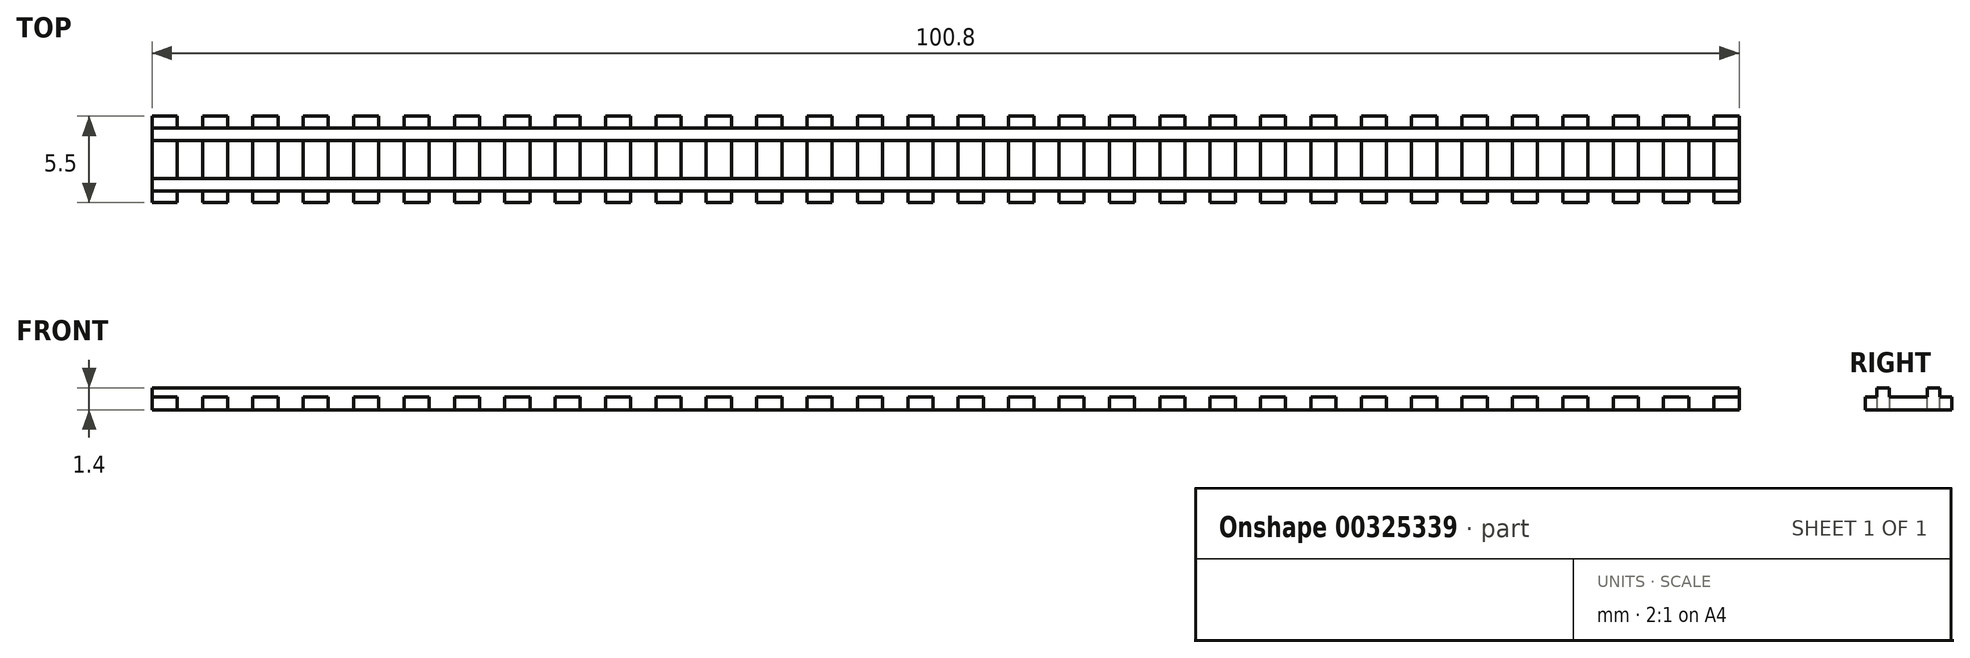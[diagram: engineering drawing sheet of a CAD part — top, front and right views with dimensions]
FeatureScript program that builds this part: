
annotation { "Feature Type Name" : "Feature", "Feature Type Description" : "" }
export const myFeature = defineFeature(function(context is Context, id is Id, definition is map)
    precondition{}
    {
        {
            var Q0;
            Q0=qCreatedBy(makeId("Top.planeOp"),FACE);
            var sketch = newSketch(context, id + "F0", { "sketchPlane" : qUnion([Q0])});
            skLineSegment(sketch, "E0.bottom", {"start": v(50.4, 2.8) * mm, "end": v(-50.4, 2.8) * mm});
            skLineSegment(sketch, "E0.top", {"start": v(50.4, 3.6) * mm, "end": v(-50.4, 3.6) * mm});
            skLineSegment(sketch, "E0.left", {"start": v(50.4, 2.8) * mm, "end": v(50.4, 3.6) * mm});
            skLineSegment(sketch, "E0.right", {"start": v(-50.4, 2.8) * mm, "end": v(-50.4, 3.6) * mm});
            skPoint(sketch, "E0.middle", {"position": v(0, 3.2) * mm});
            skLineSegment(sketch, "E1.bottom", {"start": v(50.4, -0.4) * mm, "end": v(-50.4, -0.4) * mm});
            skLineSegment(sketch, "E1.top", {"start": v(50.4, 0.4) * mm, "end": v(-50.4, 0.4) * mm});
            skLineSegment(sketch, "E1.left", {"start": v(50.4, -0.4) * mm, "end": v(50.4, 0.4) * mm});
            skLineSegment(sketch, "E1.right", {"start": v(-50.4, -0.4) * mm, "end": v(-50.4, 0.4) * mm});
            skPoint(sketch, "E1.middle", {"position": v(0, 0) * mm});
            skPoint(sketch, "E2", {"position": v(0, 1.6) * mm});
            skSolve(sketch);
        }
        {
            var Q0;
            Q0=qCreatedBy(makeId("Top.planeOp"),FACE);
            var sketch = newSketch(context, id + "F1", { "sketchPlane" : qUnion([Q0])});
            skLineSegment(sketch, "E3.bottom", {"start": v(-48.8, -1.15) * mm, "end": v(-50.4, -1.15) * mm});
            skLineSegment(sketch, "E3.top", {"start": v(-48.8, 4.35) * mm, "end": v(-50.4, 4.35) * mm});
            skLineSegment(sketch, "E3.left", {"start": v(-48.8, -1.15) * mm, "end": v(-48.8, 4.35) * mm});
            skLineSegment(sketch, "E3.right", {"start": v(-50.4, -1.15) * mm, "end": v(-50.4, 4.35) * mm});
            skPoint(sketch, "E3.middle", {"position": v(-49.6, 1.6) * mm});
            skLineSegment(sketch, "E4.1.0.0", {"start": v(-47.2, -1.15) * mm, "end": v(-47.2, 4.35) * mm});
            skLineSegment(sketch, "E4.1.0.1", {"start": v(-45.6, 4.35) * mm, "end": v(-47.2, 4.35) * mm});
            skLineSegment(sketch, "E4.1.0.2", {"start": v(-45.6, -1.15) * mm, "end": v(-45.6, 4.35) * mm});
            skLineSegment(sketch, "E4.1.0.3", {"start": v(-45.6, -1.15) * mm, "end": v(-47.2, -1.15) * mm});
            skLineSegment(sketch, "E4.2.0.0", {"start": v(-44, -1.15) * mm, "end": v(-44, 4.35) * mm});
            skLineSegment(sketch, "E4.2.0.1", {"start": v(-42.4, 4.35) * mm, "end": v(-44, 4.35) * mm});
            skLineSegment(sketch, "E4.2.0.2", {"start": v(-42.4, -1.15) * mm, "end": v(-42.4, 4.35) * mm});
            skLineSegment(sketch, "E4.2.0.3", {"start": v(-42.4, -1.15) * mm, "end": v(-44, -1.15) * mm});
            skLineSegment(sketch, "E4.3.0.0", {"start": v(-40.8, -1.15) * mm, "end": v(-40.8, 4.35) * mm});
            skLineSegment(sketch, "E4.3.0.1", {"start": v(-39.2, 4.35) * mm, "end": v(-40.8, 4.35) * mm});
            skLineSegment(sketch, "E4.3.0.2", {"start": v(-39.2, -1.15) * mm, "end": v(-39.2, 4.35) * mm});
            skLineSegment(sketch, "E4.3.0.3", {"start": v(-39.2, -1.15) * mm, "end": v(-40.8, -1.15) * mm});
            skLineSegment(sketch, "E4.4.0.0", {"start": v(-37.6, -1.15) * mm, "end": v(-37.6, 4.35) * mm});
            skLineSegment(sketch, "E4.4.0.1", {"start": v(-36, 4.35) * mm, "end": v(-37.6, 4.35) * mm});
            skLineSegment(sketch, "E4.4.0.2", {"start": v(-36, -1.15) * mm, "end": v(-36, 4.35) * mm});
            skLineSegment(sketch, "E4.4.0.3", {"start": v(-36, -1.15) * mm, "end": v(-37.6, -1.15) * mm});
            skLineSegment(sketch, "E4.5.0.0", {"start": v(-34.4, -1.15) * mm, "end": v(-34.4, 4.35) * mm});
            skLineSegment(sketch, "E4.5.0.1", {"start": v(-32.8, 4.35) * mm, "end": v(-34.4, 4.35) * mm});
            skLineSegment(sketch, "E4.5.0.2", {"start": v(-32.8, -1.15) * mm, "end": v(-32.8, 4.35) * mm});
            skLineSegment(sketch, "E4.5.0.3", {"start": v(-32.8, -1.15) * mm, "end": v(-34.4, -1.15) * mm});
            skLineSegment(sketch, "E4.6.0.0", {"start": v(-31.2, -1.15) * mm, "end": v(-31.2, 4.35) * mm});
            skLineSegment(sketch, "E4.6.0.1", {"start": v(-29.6, 4.35) * mm, "end": v(-31.2, 4.35) * mm});
            skLineSegment(sketch, "E4.6.0.2", {"start": v(-29.6, -1.15) * mm, "end": v(-29.6, 4.35) * mm});
            skLineSegment(sketch, "E4.6.0.3", {"start": v(-29.6, -1.15) * mm, "end": v(-31.2, -1.15) * mm});
            skLineSegment(sketch, "E4.7.0.0", {"start": v(-28, -1.15) * mm, "end": v(-28, 4.35) * mm});
            skLineSegment(sketch, "E4.7.0.1", {"start": v(-26.4, 4.35) * mm, "end": v(-28, 4.35) * mm});
            skLineSegment(sketch, "E4.7.0.2", {"start": v(-26.4, -1.15) * mm, "end": v(-26.4, 4.35) * mm});
            skLineSegment(sketch, "E4.7.0.3", {"start": v(-26.4, -1.15) * mm, "end": v(-28, -1.15) * mm});
            skLineSegment(sketch, "E4.8.0.0", {"start": v(-24.8, -1.15) * mm, "end": v(-24.8, 4.35) * mm});
            skLineSegment(sketch, "E4.8.0.1", {"start": v(-23.2, 4.35) * mm, "end": v(-24.8, 4.35) * mm});
            skLineSegment(sketch, "E4.8.0.2", {"start": v(-23.2, -1.15) * mm, "end": v(-23.2, 4.35) * mm});
            skLineSegment(sketch, "E4.8.0.3", {"start": v(-23.2, -1.15) * mm, "end": v(-24.8, -1.15) * mm});
            skLineSegment(sketch, "E4.9.0.0", {"start": v(-21.6, -1.15) * mm, "end": v(-21.6, 4.35) * mm});
            skLineSegment(sketch, "E4.9.0.1", {"start": v(-20, 4.35) * mm, "end": v(-21.6, 4.35) * mm});
            skLineSegment(sketch, "E4.9.0.2", {"start": v(-20, -1.15) * mm, "end": v(-20, 4.35) * mm});
            skLineSegment(sketch, "E4.9.0.3", {"start": v(-20, -1.15) * mm, "end": v(-21.6, -1.15) * mm});
            skLineSegment(sketch, "E4.10.0.0", {"start": v(-18.4, -1.15) * mm, "end": v(-18.4, 4.35) * mm});
            skLineSegment(sketch, "E4.10.0.1", {"start": v(-16.8, 4.35) * mm, "end": v(-18.4, 4.35) * mm});
            skLineSegment(sketch, "E4.10.0.2", {"start": v(-16.8, -1.15) * mm, "end": v(-16.8, 4.35) * mm});
            skLineSegment(sketch, "E4.10.0.3", {"start": v(-16.8, -1.15) * mm, "end": v(-18.4, -1.15) * mm});
            skLineSegment(sketch, "E4.11.0.0", {"start": v(-15.2, -1.15) * mm, "end": v(-15.2, 4.35) * mm});
            skLineSegment(sketch, "E4.11.0.1", {"start": v(-13.6, 4.35) * mm, "end": v(-15.2, 4.35) * mm});
            skLineSegment(sketch, "E4.11.0.2", {"start": v(-13.6, -1.15) * mm, "end": v(-13.6, 4.35) * mm});
            skLineSegment(sketch, "E4.11.0.3", {"start": v(-13.6, -1.15) * mm, "end": v(-15.2, -1.15) * mm});
            skLineSegment(sketch, "E4.12.0.0", {"start": v(-12, -1.15) * mm, "end": v(-12, 4.35) * mm});
            skLineSegment(sketch, "E4.12.0.1", {"start": v(-10.4, 4.35) * mm, "end": v(-12, 4.35) * mm});
            skLineSegment(sketch, "E4.12.0.2", {"start": v(-10.4, -1.15) * mm, "end": v(-10.4, 4.35) * mm});
            skLineSegment(sketch, "E4.12.0.3", {"start": v(-10.4, -1.15) * mm, "end": v(-12, -1.15) * mm});
            skLineSegment(sketch, "E4.13.0.0", {"start": v(-8.8, -1.15) * mm, "end": v(-8.8, 4.35) * mm});
            skLineSegment(sketch, "E4.13.0.1", {"start": v(-7.2, 4.35) * mm, "end": v(-8.8, 4.35) * mm});
            skLineSegment(sketch, "E4.13.0.2", {"start": v(-7.2, -1.15) * mm, "end": v(-7.2, 4.35) * mm});
            skLineSegment(sketch, "E4.13.0.3", {"start": v(-7.2, -1.15) * mm, "end": v(-8.8, -1.15) * mm});
            skLineSegment(sketch, "E4.14.0.0", {"start": v(-5.6, -1.15) * mm, "end": v(-5.6, 4.35) * mm});
            skLineSegment(sketch, "E4.14.0.1", {"start": v(-4, 4.35) * mm, "end": v(-5.6, 4.35) * mm});
            skLineSegment(sketch, "E4.14.0.2", {"start": v(-4, -1.15) * mm, "end": v(-4, 4.35) * mm});
            skLineSegment(sketch, "E4.14.0.3", {"start": v(-4, -1.15) * mm, "end": v(-5.6, -1.15) * mm});
            skLineSegment(sketch, "E4.15.0.0", {"start": v(-2.4, -1.15) * mm, "end": v(-2.4, 4.35) * mm});
            skLineSegment(sketch, "E4.15.0.1", {"start": v(-0.8, 4.35) * mm, "end": v(-2.4, 4.35) * mm});
            skLineSegment(sketch, "E4.15.0.2", {"start": v(-0.8, -1.15) * mm, "end": v(-0.8, 4.35) * mm});
            skLineSegment(sketch, "E4.15.0.3", {"start": v(-0.8, -1.15) * mm, "end": v(-2.4, -1.15) * mm});
            skLineSegment(sketch, "E4.16.0.0", {"start": v(0.8, -1.15) * mm, "end": v(0.8, 4.35) * mm});
            skLineSegment(sketch, "E4.16.0.1", {"start": v(2.4, 4.35) * mm, "end": v(0.8, 4.35) * mm});
            skLineSegment(sketch, "E4.16.0.2", {"start": v(2.4, -1.15) * mm, "end": v(2.4, 4.35) * mm});
            skLineSegment(sketch, "E4.16.0.3", {"start": v(2.4, -1.15) * mm, "end": v(0.8, -1.15) * mm});
            skLineSegment(sketch, "E4.17.0.0", {"start": v(4, -1.15) * mm, "end": v(4, 4.35) * mm});
            skLineSegment(sketch, "E4.17.0.1", {"start": v(5.6, 4.35) * mm, "end": v(4, 4.35) * mm});
            skLineSegment(sketch, "E4.17.0.2", {"start": v(5.6, -1.15) * mm, "end": v(5.6, 4.35) * mm});
            skLineSegment(sketch, "E4.17.0.3", {"start": v(5.6, -1.15) * mm, "end": v(4, -1.15) * mm});
            skLineSegment(sketch, "E4.18.0.0", {"start": v(7.2, -1.15) * mm, "end": v(7.2, 4.35) * mm});
            skLineSegment(sketch, "E4.18.0.1", {"start": v(8.8, 4.35) * mm, "end": v(7.2, 4.35) * mm});
            skLineSegment(sketch, "E4.18.0.2", {"start": v(8.8, -1.15) * mm, "end": v(8.8, 4.35) * mm});
            skLineSegment(sketch, "E4.18.0.3", {"start": v(8.8, -1.15) * mm, "end": v(7.2, -1.15) * mm});
            skLineSegment(sketch, "E4.19.0.0", {"start": v(10.4, -1.15) * mm, "end": v(10.4, 4.35) * mm});
            skLineSegment(sketch, "E4.19.0.1", {"start": v(12, 4.35) * mm, "end": v(10.4, 4.35) * mm});
            skLineSegment(sketch, "E4.19.0.2", {"start": v(12, -1.15) * mm, "end": v(12, 4.35) * mm});
            skLineSegment(sketch, "E4.19.0.3", {"start": v(12, -1.15) * mm, "end": v(10.4, -1.15) * mm});
            skLineSegment(sketch, "E4.direction1", {"start": v(-50.4, -1.15) * mm, "end": v(-47.2, -1.15) * mm, "construction": true});
            skLineSegment(sketch, "E5.0.20.0", {"start": v(13.6, -1.15) * mm, "end": v(13.6, 4.35) * mm});
            skLineSegment(sketch, "E5.3.20.0", {"start": v(15.2, 4.35) * mm, "end": v(13.6, 4.35) * mm});
            skLineSegment(sketch, "E5.6.20.0", {"start": v(15.2, -1.15) * mm, "end": v(15.2, 4.35) * mm});
            skLineSegment(sketch, "E5.9.20.0", {"start": v(15.2, -1.15) * mm, "end": v(13.6, -1.15) * mm});
            skLineSegment(sketch, "E5.0.21.0", {"start": v(16.8, -1.15) * mm, "end": v(16.8, 4.35) * mm});
            skLineSegment(sketch, "E5.3.21.0", {"start": v(18.4, 4.35) * mm, "end": v(16.8, 4.35) * mm});
            skLineSegment(sketch, "E5.6.21.0", {"start": v(18.4, -1.15) * mm, "end": v(18.4, 4.35) * mm});
            skLineSegment(sketch, "E5.9.21.0", {"start": v(18.4, -1.15) * mm, "end": v(16.8, -1.15) * mm});
            skLineSegment(sketch, "E5.0.22.0", {"start": v(20, -1.15) * mm, "end": v(20, 4.35) * mm});
            skLineSegment(sketch, "E5.3.22.0", {"start": v(21.6, 4.35) * mm, "end": v(20, 4.35) * mm});
            skLineSegment(sketch, "E5.6.22.0", {"start": v(21.6, -1.15) * mm, "end": v(21.6, 4.35) * mm});
            skLineSegment(sketch, "E5.9.22.0", {"start": v(21.6, -1.15) * mm, "end": v(20, -1.15) * mm});
            skLineSegment(sketch, "E5.0.23.0", {"start": v(23.2, -1.15) * mm, "end": v(23.2, 4.35) * mm});
            skLineSegment(sketch, "E5.3.23.0", {"start": v(24.8, 4.35) * mm, "end": v(23.2, 4.35) * mm});
            skLineSegment(sketch, "E5.6.23.0", {"start": v(24.8, -1.15) * mm, "end": v(24.8, 4.35) * mm});
            skLineSegment(sketch, "E5.9.23.0", {"start": v(24.8, -1.15) * mm, "end": v(23.2, -1.15) * mm});
            skLineSegment(sketch, "E5.0.24.0", {"start": v(26.4, -1.15) * mm, "end": v(26.4, 4.35) * mm});
            skLineSegment(sketch, "E5.3.24.0", {"start": v(28, 4.35) * mm, "end": v(26.4, 4.35) * mm});
            skLineSegment(sketch, "E5.6.24.0", {"start": v(28, -1.15) * mm, "end": v(28, 4.35) * mm});
            skLineSegment(sketch, "E5.9.24.0", {"start": v(28, -1.15) * mm, "end": v(26.4, -1.15) * mm});
            skLineSegment(sketch, "E5.0.25.0", {"start": v(29.6, -1.15) * mm, "end": v(29.6, 4.35) * mm});
            skLineSegment(sketch, "E5.3.25.0", {"start": v(31.2, 4.35) * mm, "end": v(29.6, 4.35) * mm});
            skLineSegment(sketch, "E5.6.25.0", {"start": v(31.2, -1.15) * mm, "end": v(31.2, 4.35) * mm});
            skLineSegment(sketch, "E5.9.25.0", {"start": v(31.2, -1.15) * mm, "end": v(29.6, -1.15) * mm});
            skLineSegment(sketch, "E5.0.26.0", {"start": v(32.8, -1.15) * mm, "end": v(32.8, 4.35) * mm});
            skLineSegment(sketch, "E5.3.26.0", {"start": v(34.4, 4.35) * mm, "end": v(32.8, 4.35) * mm});
            skLineSegment(sketch, "E5.6.26.0", {"start": v(34.4, -1.15) * mm, "end": v(34.4, 4.35) * mm});
            skLineSegment(sketch, "E5.9.26.0", {"start": v(34.4, -1.15) * mm, "end": v(32.8, -1.15) * mm});
            skLineSegment(sketch, "E5.0.27.0", {"start": v(36, -1.15) * mm, "end": v(36, 4.35) * mm});
            skLineSegment(sketch, "E5.3.27.0", {"start": v(37.6, 4.35) * mm, "end": v(36, 4.35) * mm});
            skLineSegment(sketch, "E5.6.27.0", {"start": v(37.6, -1.15) * mm, "end": v(37.6, 4.35) * mm});
            skLineSegment(sketch, "E5.9.27.0", {"start": v(37.6, -1.15) * mm, "end": v(36, -1.15) * mm});
            skLineSegment(sketch, "E5.0.28.0", {"start": v(39.2, -1.15) * mm, "end": v(39.2, 4.35) * mm});
            skLineSegment(sketch, "E5.3.28.0", {"start": v(40.8, 4.35) * mm, "end": v(39.2, 4.35) * mm});
            skLineSegment(sketch, "E5.6.28.0", {"start": v(40.8, -1.15) * mm, "end": v(40.8, 4.35) * mm});
            skLineSegment(sketch, "E5.9.28.0", {"start": v(40.8, -1.15) * mm, "end": v(39.2, -1.15) * mm});
            skLineSegment(sketch, "E5.0.29.0", {"start": v(42.4, -1.15) * mm, "end": v(42.4, 4.35) * mm});
            skLineSegment(sketch, "E5.3.29.0", {"start": v(44, 4.35) * mm, "end": v(42.4, 4.35) * mm});
            skLineSegment(sketch, "E5.6.29.0", {"start": v(44, -1.15) * mm, "end": v(44, 4.35) * mm});
            skLineSegment(sketch, "E5.9.29.0", {"start": v(44, -1.15) * mm, "end": v(42.4, -1.15) * mm});
            skLineSegment(sketch, "E6.0.30.0", {"start": v(45.6, -1.15) * mm, "end": v(45.6, 4.35) * mm});
            skLineSegment(sketch, "E6.3.30.0", {"start": v(47.2, 4.35) * mm, "end": v(45.6, 4.35) * mm});
            skLineSegment(sketch, "E6.6.30.0", {"start": v(47.2, -1.15) * mm, "end": v(47.2, 4.35) * mm});
            skLineSegment(sketch, "E6.9.30.0", {"start": v(47.2, -1.15) * mm, "end": v(45.6, -1.15) * mm});
            skLineSegment(sketch, "E6.0.31.0", {"start": v(48.8, -1.15) * mm, "end": v(48.8, 4.35) * mm});
            skLineSegment(sketch, "E6.3.31.0", {"start": v(50.4, 4.35) * mm, "end": v(48.8, 4.35) * mm});
            skLineSegment(sketch, "E6.6.31.0", {"start": v(50.4, -1.15) * mm, "end": v(50.4, 4.35) * mm});
            skLineSegment(sketch, "E6.9.31.0", {"start": v(50.4, -1.15) * mm, "end": v(48.8, -1.15) * mm});
            skSolve(sketch);
        }
        {
            var Q0;
            Q0=makeQuery(id+"F0.imprint","IMPRINT",FACE,{"disambiguationData":[TD([[makeQuery(id+"F0.imprint","IMPRINT",EDGE,{"derivedFrom":sQuery(id+"F0.wireOp",EDGE,"E1.bottom")}),-1.0]])]});
            extrude(context, id + "F2", {"entities" : qUnion([Q0]), "depth" : 1.4 * mm});
        }
        {
            var Q0;
            Q0=makeQuery(id+"F1.imprint","IMPRINT",FACE,{"disambiguationData":[TD([[makeQuery(id+"F1.imprint","IMPRINT",EDGE,{"derivedFrom":sQuery(id+"F1.wireOp",EDGE,"E4.10.0.0")}),-1.0]])]});
            var Q1;
            Q1=makeQuery(id+"F1.imprint","IMPRINT",FACE,{"disambiguationData":[TD([[makeQuery(id+"F1.imprint","IMPRINT",EDGE,{"derivedFrom":sQuery(id+"F1.wireOp",EDGE,"E4.6.0.0")}),-1.0]])]});
            var Q2;
            Q2=makeQuery(id+"F1.imprint","IMPRINT",FACE,{"disambiguationData":[TD([[makeQuery(id+"F1.imprint","IMPRINT",EDGE,{"derivedFrom":sQuery(id+"F1.wireOp",EDGE,"E5.0.20.0")}),-1.0]])]});
            var Q3;
            Q3=makeQuery(id+"F1.imprint","IMPRINT",FACE,{"disambiguationData":[TD([[makeQuery(id+"F1.imprint","IMPRINT",EDGE,{"derivedFrom":sQuery(id+"F1.wireOp",EDGE,"E5.0.26.0")}),-1.0]])]});
            var Q4;
            Q4=makeQuery(id+"F1.imprint","IMPRINT",FACE,{"disambiguationData":[TD([[makeQuery(id+"F1.imprint","IMPRINT",EDGE,{"derivedFrom":sQuery(id+"F1.wireOp",EDGE,"E5.0.27.0")}),-1.0]])]});
            var Q5;
            Q5=makeQuery(id+"F1.imprint","IMPRINT",FACE,{"disambiguationData":[TD([[makeQuery(id+"F1.imprint","IMPRINT",EDGE,{"derivedFrom":sQuery(id+"F1.wireOp",EDGE,"E4.9.0.0")}),-1.0]])]});
            var Q6;
            Q6=makeQuery(id+"F1.imprint","IMPRINT",FACE,{"disambiguationData":[TD([[makeQuery(id+"F1.imprint","IMPRINT",EDGE,{"derivedFrom":sQuery(id+"F1.wireOp",EDGE,"E4.3.0.0")}),-1.0]])]});
            var Q7;
            Q7=makeQuery(id+"F1.imprint","IMPRINT",FACE,{"disambiguationData":[TD([[makeQuery(id+"F1.imprint","IMPRINT",EDGE,{"derivedFrom":sQuery(id+"F1.wireOp",EDGE,"E5.0.21.0")}),-1.0]])]});
            var Q8;
            Q8=makeQuery(id+"F1.imprint","IMPRINT",FACE,{"disambiguationData":[TD([[makeQuery(id+"F1.imprint","IMPRINT",EDGE,{"derivedFrom":sQuery(id+"F1.wireOp",EDGE,"E6.0.30.0")}),-1.0]])]});
            var Q9;
            Q9=makeQuery(id+"F1.imprint","IMPRINT",FACE,{"disambiguationData":[TD([[makeQuery(id+"F1.imprint","IMPRINT",EDGE,{"derivedFrom":sQuery(id+"F1.wireOp",EDGE,"E5.0.24.0")}),-1.0]])]});
            var Q10;
            Q10=makeQuery(id+"F1.imprint","IMPRINT",FACE,{"disambiguationData":[TD([[makeQuery(id+"F1.imprint","IMPRINT",EDGE,{"derivedFrom":sQuery(id+"F1.wireOp",EDGE,"E4.4.0.0")}),-1.0]])]});
            var Q11;
            Q11=makeQuery(id+"F1.imprint","IMPRINT",FACE,{"disambiguationData":[TD([[makeQuery(id+"F1.imprint","IMPRINT",EDGE,{"derivedFrom":sQuery(id+"F1.wireOp",EDGE,"E6.0.31.0")}),-1.0]])]});
            var Q12;
            Q12=makeQuery(id+"F1.imprint","IMPRINT",FACE,{"disambiguationData":[TD([[makeQuery(id+"F1.imprint","IMPRINT",EDGE,{"derivedFrom":sQuery(id+"F1.wireOp",EDGE,"E5.0.29.0")}),-1.0]])]});
            var Q13;
            Q13=makeQuery(id+"F1.imprint","IMPRINT",FACE,{"disambiguationData":[TD([[makeQuery(id+"F1.imprint","IMPRINT",EDGE,{"derivedFrom":sQuery(id+"F1.wireOp",EDGE,"E4.8.0.0")}),-1.0]])]});
            var Q14;
            Q14=makeQuery(id+"F1.imprint","IMPRINT",FACE,{"disambiguationData":[TD([[makeQuery(id+"F1.imprint","IMPRINT",EDGE,{"derivedFrom":sQuery(id+"F1.wireOp",EDGE,"E4.18.0.0")}),-1.0]])]});
            var Q15;
            Q15=makeQuery(id+"F1.imprint","IMPRINT",FACE,{"disambiguationData":[TD([[makeQuery(id+"F1.imprint","IMPRINT",EDGE,{"derivedFrom":sQuery(id+"F1.wireOp",EDGE,"E4.11.0.0")}),-1.0]])]});
            var Q16;
            Q16=makeQuery(id+"F1.imprint","IMPRINT",FACE,{"disambiguationData":[TD([[makeQuery(id+"F1.imprint","IMPRINT",EDGE,{"derivedFrom":sQuery(id+"F1.wireOp",EDGE,"E4.1.0.0")}),-1.0]])]});
            var Q17;
            Q17=makeQuery(id+"F1.imprint","IMPRINT",FACE,{"disambiguationData":[TD([[makeQuery(id+"F1.imprint","IMPRINT",EDGE,{"derivedFrom":sQuery(id+"F1.wireOp",EDGE,"E4.2.0.0")}),-1.0]])]});
            var Q18;
            Q18=makeQuery(id+"F1.imprint","IMPRINT",FACE,{"disambiguationData":[TD([[makeQuery(id+"F1.imprint","IMPRINT",EDGE,{"derivedFrom":sQuery(id+"F1.wireOp",EDGE,"E4.14.0.0")}),-1.0]])]});
            var Q19;
            Q19=makeQuery(id+"F1.imprint","IMPRINT",FACE,{"disambiguationData":[TD([[makeQuery(id+"F1.imprint","IMPRINT",EDGE,{"derivedFrom":sQuery(id+"F1.wireOp",EDGE,"E4.19.0.0")}),-1.0]])]});
            var Q20;
            Q20=makeQuery(id+"F1.imprint","IMPRINT",FACE,{"disambiguationData":[TD([[makeQuery(id+"F1.imprint","IMPRINT",EDGE,{"derivedFrom":sQuery(id+"F1.wireOp",EDGE,"E4.7.0.0")}),-1.0]])]});
            var Q21;
            Q21=makeQuery(id+"F1.imprint","IMPRINT",FACE,{"disambiguationData":[TD([[makeQuery(id+"F1.imprint","IMPRINT",EDGE,{"derivedFrom":sQuery(id+"F1.wireOp",EDGE,"E4.5.0.0")}),-1.0]])]});
            var Q22;
            Q22=makeQuery(id+"F1.imprint","IMPRINT",FACE,{"disambiguationData":[TD([[makeQuery(id+"F1.imprint","IMPRINT",EDGE,{"derivedFrom":sQuery(id+"F1.wireOp",EDGE,"E5.0.28.0")}),-1.0]])]});
            var Q23;
            Q23=makeQuery(id+"F1.imprint","IMPRINT",FACE,{"disambiguationData":[TD([[makeQuery(id+"F1.imprint","IMPRINT",EDGE,{"derivedFrom":sQuery(id+"F1.wireOp",EDGE,"E4.13.0.0")}),-1.0]])]});
            var Q24;
            Q24=makeQuery(id+"F1.imprint","IMPRINT",FACE,{"disambiguationData":[TD([[makeQuery(id+"F1.imprint","IMPRINT",EDGE,{"derivedFrom":sQuery(id+"F1.wireOp",EDGE,"E5.0.25.0")}),-1.0]])]});
            var Q25;
            Q25=makeQuery(id+"F1.imprint","IMPRINT",FACE,{"disambiguationData":[TD([[makeQuery(id+"F1.imprint","IMPRINT",EDGE,{"derivedFrom":sQuery(id+"F1.wireOp",EDGE,"E5.0.22.0")}),-1.0]])]});
            var Q26;
            Q26=makeQuery(id+"F1.imprint","IMPRINT",FACE,{"disambiguationData":[TD([[makeQuery(id+"F1.imprint","IMPRINT",EDGE,{"derivedFrom":sQuery(id+"F1.wireOp",EDGE,"E4.17.0.0")}),-1.0]])]});
            var Q27;
            Q27=makeQuery(id+"F1.imprint","IMPRINT",FACE,{"disambiguationData":[TD([[makeQuery(id+"F1.imprint","IMPRINT",EDGE,{"derivedFrom":sQuery(id+"F1.wireOp",EDGE,"E4.15.0.0")}),-1.0]])]});
            var Q28;
            Q28=makeQuery(id+"F1.imprint","IMPRINT",FACE,{"disambiguationData":[TD([[makeQuery(id+"F1.imprint","IMPRINT",EDGE,{"derivedFrom":sQuery(id+"F1.wireOp",EDGE,"E3.bottom")}),-1.0]])]});
            var Q29;
            Q29=makeQuery(id+"F1.imprint","IMPRINT",FACE,{"disambiguationData":[TD([[makeQuery(id+"F1.imprint","IMPRINT",EDGE,{"derivedFrom":sQuery(id+"F1.wireOp",EDGE,"E5.0.23.0")}),-1.0]])]});
            var Q30;
            Q30=makeQuery(id+"F1.imprint","IMPRINT",FACE,{"disambiguationData":[TD([[makeQuery(id+"F1.imprint","IMPRINT",EDGE,{"derivedFrom":sQuery(id+"F1.wireOp",EDGE,"E4.12.0.0")}),-1.0]])]});
            var Q31;
            Q31=makeQuery(id+"F1.imprint","IMPRINT",FACE,{"disambiguationData":[TD([[makeQuery(id+"F1.imprint","IMPRINT",EDGE,{"derivedFrom":sQuery(id+"F1.wireOp",EDGE,"E4.16.0.0")}),-1.0]])]});
            extrude(context, id + "F3", {"entities" : qUnion([Q0, Q1, Q2, Q3, Q4, Q5, Q6, Q7, Q8, Q9, Q10, Q11, Q12, Q13, Q14, Q15, Q16, Q17, Q18, Q19, Q20, Q21, Q22, Q23, Q24, Q25, Q26, Q27, Q28, Q29, Q30, Q31]), "operationType" : NewBodyOperationType.ADD, "depth" : .8 * mm});
        }
        {
            var Q0;
            Q0=makeQuery(id+"F0.imprint","IMPRINT",FACE,{"disambiguationData":[TD([[makeQuery(id+"F0.imprint","IMPRINT",EDGE,{"derivedFrom":sQuery(id+"F0.wireOp",EDGE,"E0.bottom")}),-1.0]])]});
            extrude(context, id + "F4", {"entities" : qUnion([Q0]), "operationType" : NewBodyOperationType.ADD, "depth" : 1.4 * mm});
        }
    });
